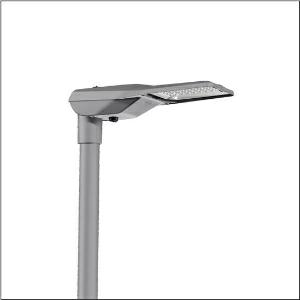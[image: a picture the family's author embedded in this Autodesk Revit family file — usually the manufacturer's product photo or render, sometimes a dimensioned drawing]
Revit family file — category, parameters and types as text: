
# Revit family: streetlight_sl_21_iq_mini___st1_0a_5xe2d31y08jb_55ca
name_source: partatom
category: Lighting Fixtures
units: mm (PartAtom-declared; Revit-internal decimal feet)

## family parameters
Cut with Voids When Loaded = No
Host = Face
Light Source = No
Part Type = Normal
Room Calculation Point = No
Round Connector Dimension = Use Diameter
Shared = No

## types (1)
- --- (1 x LED, 11210 lm, 72.5 W, 3000K)
    Apparent Load = 73 VA
    CIE Flux Codes = 40 73 97 100 100
    Color Rendering = 70
    Color Temperature = 3000K
    Default Elevation = 1800 mm
    Description = Streetlight SL 21 iQ mini, mast luminaire, primary light control with lens, of PMMA, primary optical cover: cover, of toughened safety glass, transparent, light distribution: ST1.0a, light emission: direct distribution, primary light characteristic: asymmetric, installation type: post-top, side-entry, LED, High Power LED, rated luminous flux: 11.210lm, luminous efficacy: 155lm/W, light colour: 730, colour temperature: 3000K, control: presetting dimming logarithmic, Street-Remote, Auto-Match, Temp-Guard, Lumen-Switch, Night-Set, Smart-Wire, Light-Fading, Desk-Remote (wireless, voltage-free reading and setting of iQ features in the workshop via application-optimized NFC function/RFID function), optimised constant luminous flux control (CLO 2.0), mains connection: 220..240V, AC, 50/60Hz, start of lifetime: 73W, end of service life: 76W, reduction: 33W, luminaire housing, of diecast aluminium, powder-coated, Siteco® metallic grey (DB 702S), corrosivity category C5 mid according to DIN EN ISO 12944, please order mast flange separately, inclination adjustable: 0°, 5°, 10°, 15°, sealing non-destructively replaceable, multi-level sealing system, length: 628mm, width: 235mm, height: 110mm, mast flange for spigot size: 42mm (side-entry): 5XC10008XM4, 60/48mm (side-entry/post-top): 5XC10108XM2, 76/60mm (side-entry/post-top): 5XC10108XM1, Smart Interface below and above, protection rating (complete): IP66, insulation class (complete): insulation class II (safety insulation), certification: CE, ENEC, ENEC+, VDE, impact resistance: IK09, permissible operating ambient temperature for outdoor applications: -40..+50°C, standard-compliant lighting for roads and squares, packaging unit: 1 piece

Light Distribution: ST1.0a
    Height = 110 mm
    Lamp = 1 x LED
    Lamp Light Flux = 11210 lm
    Lamp Power = 72.5 W
    Lamp count = 1
    Length = 625 mm
    Luminous efficacy = 155 lm/W
    Manufacturer = Siteco
    ModVariant = No
    Model = 5XE2D31Y08JB
    Number of Poles = 1
    OnlyDefault = Yes
    Power Factor = 1
    Product Name = Streetlight SL 21 iQ mini | ST1.0a
    Product group = mast luminaire | pylon top
    ProductGroupID = 6100
    Protection Class = Protection class II
    Protection Degree = IP 66
    RLX_Detail_Level = 1
    RLX_Emergency_Light_Flux = 0 lm
    RLX_Emergency_Type = 0
    RLX_Emergency_Type_DB = No
    RlxData = <blob elided: 92677 chars, md5=c0101e7d>
    Socket = socket
    Standby Power = 0 W
    System Light Flux = 11210 lm
    System Power = 73 W
    Type Comments = factory setting: luminous flux: 100 % | dim-lin: 254 | 755 mA
    Type Image = l_1003514.jpg
    URL = http://relux.com
    VarID = @adj_044111
    Voltage = 0 V
    Weight = 0.00 kg
    Width = 234 mm

## geometry (parser evidence)
native form markers: Blend x4, Sweep x11
no freeform markers — native parametric forms only
